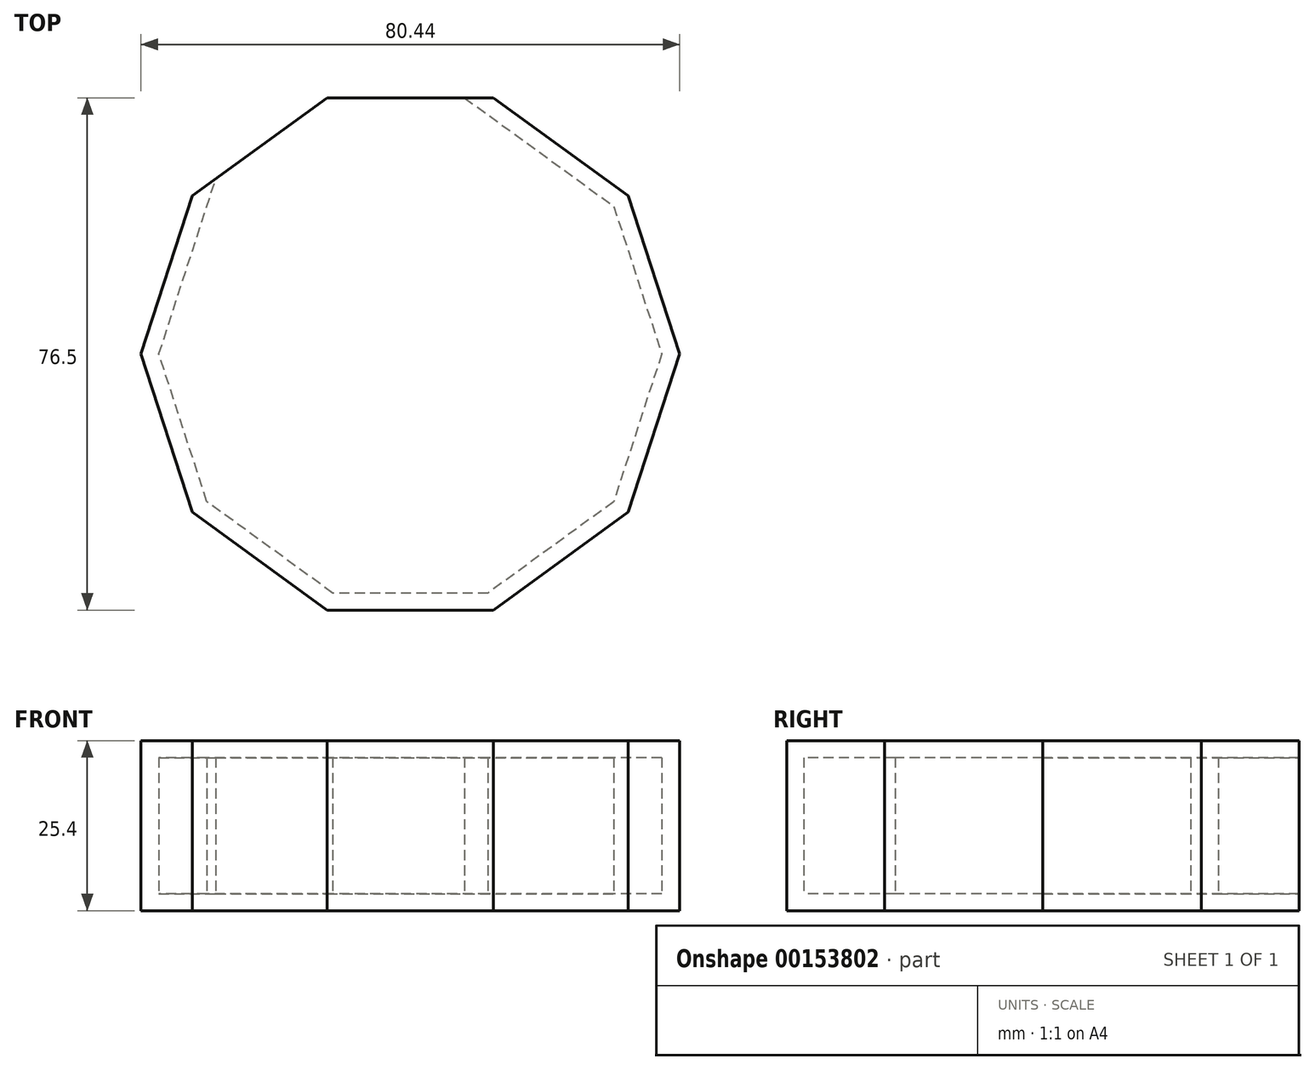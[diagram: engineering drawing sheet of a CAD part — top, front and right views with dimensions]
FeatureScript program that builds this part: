
annotation { "Feature Type Name" : "Feature", "Feature Type Description" : "" }
export const myFeature = defineFeature(function(context is Context, id is Id, definition is map)
    precondition{}
    {
        {
            var Q0;
            Q0=qCreatedBy(makeId("Top.planeOp"),FACE);
            var sketch = newSketch(context, id + "F0", { "sketchPlane" : qUnion([Q0])});
            skCircle(sketch, "E0.cCircle", {"center": v(0, 38.25) * mm, "radius": 38.25 * mm, "construction": true});
            skLineSegment(sketch, "E0.0", {"start": v(12.43, 0) * mm, "end": v(-12.43, 0) * mm});
            skLineSegment(sketch, "E0.1", {"start": v(-12.43, 0) * mm, "end": v(-32.54, 14.61) * mm});
            skLineSegment(sketch, "E0.2", {"start": v(-32.54, 14.61) * mm, "end": v(-40.22, 38.25) * mm});
            skLineSegment(sketch, "E0.3", {"start": v(-40.22, 38.25) * mm, "end": v(-32.54, 61.9) * mm});
            skLineSegment(sketch, "E0.4", {"start": v(-32.54, 61.9) * mm, "end": v(-12.43, 76.5) * mm});
            skLineSegment(sketch, "E0.5", {"start": v(-12.43, 76.5) * mm, "end": v(12.43, 76.5) * mm});
            skLineSegment(sketch, "E0.6", {"start": v(12.43, 76.5) * mm, "end": v(32.54, 61.9) * mm});
            skLineSegment(sketch, "E0.7", {"start": v(32.54, 61.9) * mm, "end": v(40.22, 38.25) * mm});
            skLineSegment(sketch, "E0.8", {"start": v(40.22, 38.25) * mm, "end": v(32.54, 14.61) * mm});
            skLineSegment(sketch, "E0.9", {"start": v(32.54, 14.61) * mm, "end": v(12.43, 0) * mm});
            skPoint(sketch, "E0.0.midPoint", {"position": v(0, 0) * mm});
            skSolve(sketch);
        }
        {
            var Q0;
            Q0=makeQuery(id+"F0.imprint","IMPRINT",FACE,{"disambiguationData":[TD([[makeQuery(id+"F0.imprint","IMPRINT",EDGE,{"derivedFrom":sQuery(id+"F0.wireOp",EDGE,"E0.0")}),-1.0]])]});
            extrude(context, id + "F1", {"entities" : qUnion([Q0]), "depth" : 25.4 * mm});
        }
        {
            var Q0;
            Q0=makeQuery(id+"F1.opExtrude","SWEPT_FACE",FACE,{"disambiguationData":[OSD([sQuery(id+"F0.wireOp",EDGE,"E0.4")])]});
            var Q1;
            Q1=makeQuery(id+"F1.opExtrude","SWEPT_FACE",FACE,{"disambiguationData":[OSD([sQuery(id+"F0.wireOp",EDGE,"E0.5")])]});
            shell(context, id + "F2", {"entities" : qUnion([Q0, Q1]), "thickness" : 2.54 * mm});
        }
    });
